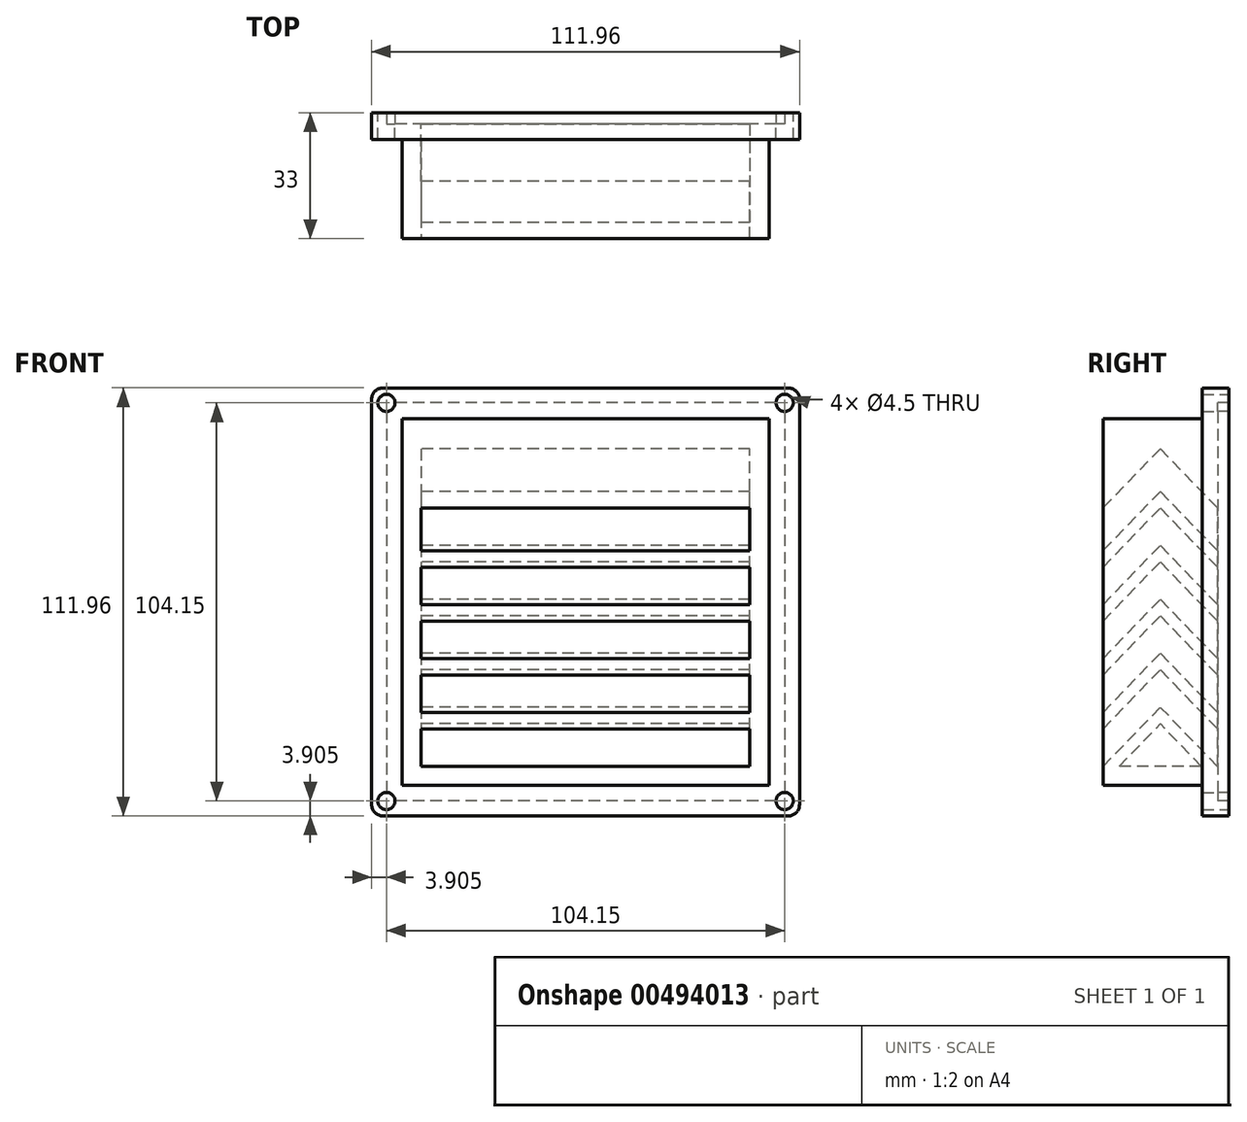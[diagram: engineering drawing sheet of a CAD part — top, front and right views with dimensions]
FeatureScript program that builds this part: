
annotation { "Feature Type Name" : "Feature", "Feature Type Description" : "" }
export const myFeature = defineFeature(function(context is Context, id is Id, definition is map)
    precondition{}
    {
        {
            var Q0;
            Q0=qCreatedBy(makeId("Front.planeOp"),FACE);
            var sketch = newSketch(context, id + "F0", { "sketchPlane" : qUnion([Q0])});
            skPoint(sketch, "E0.middle", {"position": v(0, 0) * mm});
            skCircle(sketch, "E1", {"center": v(-52.08, 52.08) * mm, "radius": 2.25 * mm});
            skCircle(sketch, "E2", {"center": v(52.08, 52.08) * mm, "radius": 2.25 * mm});
            skCircle(sketch, "E3", {"center": v(-52.08, -52.08) * mm, "radius": 2.25 * mm});
            skCircle(sketch, "E4", {"center": v(52.07, -52.08) * mm, "radius": 2.25 * mm});
            skLineSegment(sketch, "E5.bottom", {"start": v(-52.07, 52.08) * mm, "end": v(52.07, 52.08) * mm});
            skLineSegment(sketch, "E5.top", {"start": v(-52.07, -52.08) * mm, "end": v(52.07, -52.08) * mm});
            skLineSegment(sketch, "E5.left", {"start": v(-52.08, 52.08) * mm, "end": v(-52.08, -52.08) * mm});
            skLineSegment(sketch, "E5.right", {"start": v(52.07, 52.08) * mm, "end": v(52.07, -52.08) * mm});
            skLineSegment(sketch, "E6.0", {"start": v(-52.98, 55.98) * mm, "end": v(52.98, 55.98) * mm});
            skLineSegment(sketch, "E6.1", {"start": v(-55.98, 52.98) * mm, "end": v(-55.98, -52.98) * mm});
            skLineSegment(sketch, "E6.2", {"start": v(-52.98, -55.98) * mm, "end": v(52.98, -55.98) * mm});
            skLineSegment(sketch, "E6.3", {"start": v(55.98, 52.98) * mm, "end": v(55.98, -52.98) * mm});
            skPoint(sketch, "E7.visualSharp", {"position": v(-55.98, 55.98) * mm});
            skArc(sketch, "E7.filletArc", {"start": v(-52.98, 55.98) * mm, "mid": v(-55.1, 55.1) * mm, "end": v(-55.98, 52.98) * mm});
            skPoint(sketch, "E8.visualSharp", {"position": v(55.98, 55.98) * mm});
            skArc(sketch, "E8.filletArc", {"start": v(55.98, 52.98) * mm, "mid": v(55.1, 55.1) * mm, "end": v(52.98, 55.98) * mm});
            skPoint(sketch, "E9.visualSharp", {"position": v(55.98, -55.98) * mm});
            skArc(sketch, "E9.filletArc", {"start": v(52.98, -55.98) * mm, "mid": v(55.1, -55.1) * mm, "end": v(55.98, -52.98) * mm});
            skPoint(sketch, "E10.visualSharp", {"position": v(-55.98, -55.98) * mm});
            skArc(sketch, "E10.filletArc", {"start": v(-55.98, -52.98) * mm, "mid": v(-55.1, -55.1) * mm, "end": v(-52.98, -55.98) * mm});
            skLineSegment(sketch, "E11.0", {"start": v(-47.97, 47.97) * mm, "end": v(47.97, 47.97) * mm});
            skLineSegment(sketch, "E11.1", {"start": v(-47.97, 47.97) * mm, "end": v(-47.97, -47.97) * mm});
            skLineSegment(sketch, "E11.2", {"start": v(-47.97, -47.97) * mm, "end": v(47.97, -47.97) * mm});
            skLineSegment(sketch, "E11.3", {"start": v(47.97, 47.97) * mm, "end": v(47.97, -47.97) * mm});
            skSolve(sketch);
        }
        {
            var Q0;
            Q0=makeQuery(id+"F0.imprint","IMPRINT",FACE,{"disambiguationData":[TD([[makeQuery(id+"F0.imprint","IMPRINT",EDGE,{"derivedFrom":sQuery(id+"F0.wireOp",EDGE,"E6.0")}),-1.0]])]});
            var Q1;
            {var subQ5=sQuery(id+"F0.wireOp",EDGE,"E1");var subQ7=sQuery(id+"F0.wireOp",EDGE,"E5.bottom");var subQ15=makeQuery(id+"F0.imprint","INTERSECT",VERTEX,{"derivedFrom":[subQ5,subQ7]});Q1=makeQuery(id+"F0.imprint","IMPRINT",FACE,{"disambiguationData":[TD([[makeQuery(id+"F0.imprint","IMPRINT",EDGE,{"disambiguationData":[TD([[subQ15,1.0]])],"derivedFrom":subQ5}),-1.0]])]});}
            extrude(context, id + "F1", {"entities" : qUnion([Q0, Q1]), "depth" : 4 * mm});
        }
        {
            var Q0;
            Q0=makeQuery(id+"F0.imprint","IMPRINT",FACE,{"disambiguationData":[TD([[makeQuery(id+"F0.imprint","IMPRINT",EDGE,{"derivedFrom":sQuery(id+"F0.wireOp",EDGE,"E11.0")}),-1.0]])]});
            extrude(context, id + "F2", {"entities" : qUnion([Q0]), "operationType" : NewBodyOperationType.ADD, "depth" : 30 * mm});
        }
        {
            var Q0;
            Q0=makeQuery(id+"F2.opExtrude","CAP_FACE",FACE,{"disambiguationData":[OSD([sQuery(id+"F0.wireOp",EDGE,"E11.0"),sQuery(id+"F0.wireOp",EDGE,"E11.1"),sQuery(id+"F0.wireOp",EDGE,"E11.2"),sQuery(id+"F0.wireOp",EDGE,"E11.3")])],"isStart":false});
            var sketch = newSketch(context, id + "F3", { "sketchPlane" : qUnion([Q0])});
            skLineSegment(sketch, "E12.0", {"start": v(42.97, -42.97) * mm, "end": v(42.97, 42.97) * mm});
            skLineSegment(sketch, "E12.1", {"start": v(-42.97, -42.97) * mm, "end": v(42.97, -42.97) * mm});
            skLineSegment(sketch, "E12.2", {"start": v(-42.97, 42.97) * mm, "end": v(-42.97, -42.97) * mm});
            skLineSegment(sketch, "E12.3", {"start": v(42.97, 42.97) * mm, "end": v(-42.97, 42.97) * mm});
            skSolve(sketch);
        }
        {
            var Q0;
            Q0=makeQuery(id+"F3.imprint","IMPRINT",FACE,{"disambiguationData":[TD([[makeQuery(id+"F3.imprint","IMPRINT",EDGE,{"derivedFrom":sQuery(id+"F3.wireOp",EDGE,"E12.0")}),1.0]])]});
            extrude(context, id + "F4", {"entities" : qUnion([Q0]), "operationType" : NewBodyOperationType.REMOVE, "oppositeDirection" : true, "depth" : 40 * mm});
        }
        {
            var Q0;
            Q0=makeQuery(id+"F4.boolean.opBoolean","COPY",FACE,{"derivedFrom":makeQuery(id+"F4.opExtrude","SWEPT_FACE",FACE,{"disambiguationData":[OSD([sQuery(id+"F3.wireOp",EDGE,"E12.2")])]})});
            var sketch = newSketch(context, id + "F5", { "sketchPlane" : qUnion([Q0])});
            skLineSegment(sketch, "E13", {"start": v(-15, 44.38) * mm, "end": v(-30, 28.88) * mm});
            skLineSegment(sketch, "E14", {"start": v(-30, 27.47) * mm, "end": v(-30, 23.12) * mm});
            skLineSegment(sketch, "E15", {"start": v(-15, 40.03) * mm, "end": v(-30, 24.52) * mm});
            skLineSegment(sketch, "E16.MirrorCS", {"start": v(0, 28.88) * mm, "end": v(0, 24.52) * mm});
            skLineSegment(sketch, "E17.MirrorCS", {"start": v(-15, 44.38) * mm, "end": v(0, 28.88) * mm});
            skLineSegment(sketch, "E18.MirrorCS", {"start": v(-15, 40.03) * mm, "end": v(0, 24.52) * mm});
            skLineSegment(sketch, "E19.1.0.0", {"start": v(-15, 28.88) * mm, "end": v(-30, 13.37) * mm});
            skLineSegment(sketch, "E19.1.0.1", {"start": v(-15, 28.88) * mm, "end": v(0, 13.37) * mm});
            skLineSegment(sketch, "E19.1.0.2", {"start": v(-15, 24.52) * mm, "end": v(-30, 9.02) * mm});
            skLineSegment(sketch, "E19.1.0.3", {"start": v(-15, 24.52) * mm, "end": v(0, 9.02) * mm});
            skLineSegment(sketch, "E19.1.0.4", {"start": v(-30, 13.37) * mm, "end": v(-30, 9.02) * mm});
            skLineSegment(sketch, "E19.1.0.5", {"start": v(0, 13.37) * mm, "end": v(0, 9.02) * mm});
            skLineSegment(sketch, "E19.2.0.0", {"start": v(-15, 14.78) * mm, "end": v(-30, -0.73) * mm});
            skLineSegment(sketch, "E19.2.0.1", {"start": v(-15, 14.78) * mm, "end": v(0, -0.73) * mm});
            skLineSegment(sketch, "E19.2.0.2", {"start": v(-15, 10.42) * mm, "end": v(-30, -5.08) * mm});
            skLineSegment(sketch, "E19.2.0.3", {"start": v(-15, 10.42) * mm, "end": v(0, -5.08) * mm});
            skLineSegment(sketch, "E19.2.0.4", {"start": v(-30, -0.73) * mm, "end": v(-30, -5.08) * mm});
            skLineSegment(sketch, "E19.2.0.5", {"start": v(0, -0.73) * mm, "end": v(0, -5.08) * mm});
            skLineSegment(sketch, "E19.3.0.0", {"start": v(-15, 0.68) * mm, "end": v(-30, -14.83) * mm});
            skLineSegment(sketch, "E19.3.0.1", {"start": v(-15, 0.68) * mm, "end": v(0, -14.83) * mm});
            skLineSegment(sketch, "E19.3.0.2", {"start": v(-15, -3.68) * mm, "end": v(-30, -19.18) * mm});
            skLineSegment(sketch, "E19.3.0.3", {"start": v(-15, -3.68) * mm, "end": v(0, -19.18) * mm});
            skLineSegment(sketch, "E19.3.0.4", {"start": v(-30, -14.83) * mm, "end": v(-30, -19.18) * mm});
            skLineSegment(sketch, "E19.3.0.5", {"start": v(0, -14.83) * mm, "end": v(0, -19.18) * mm});
            skLineSegment(sketch, "E19.4.0.0", {"start": v(-15, -13.42) * mm, "end": v(-30, -28.93) * mm});
            skLineSegment(sketch, "E19.4.0.1", {"start": v(-15, -13.42) * mm, "end": v(0, -28.93) * mm});
            skLineSegment(sketch, "E19.4.0.2", {"start": v(-15, -17.78) * mm, "end": v(-30, -33.28) * mm});
            skLineSegment(sketch, "E19.4.0.3", {"start": v(-15, -17.78) * mm, "end": v(0, -33.28) * mm});
            skLineSegment(sketch, "E19.4.0.4", {"start": v(-30, -28.93) * mm, "end": v(-30, -33.28) * mm});
            skLineSegment(sketch, "E19.4.0.5", {"start": v(0, -28.93) * mm, "end": v(0, -33.28) * mm});
            skLineSegment(sketch, "E19.5.0.0", {"start": v(-15, -27.52) * mm, "end": v(-30, -43.03) * mm});
            skLineSegment(sketch, "E19.5.0.1", {"start": v(-15, -27.52) * mm, "end": v(0, -43.03) * mm});
            skLineSegment(sketch, "E19.5.0.2", {"start": v(-15, -31.88) * mm, "end": v(-30, -47.38) * mm});
            skLineSegment(sketch, "E19.5.0.3", {"start": v(-15, -31.88) * mm, "end": v(0, -47.38) * mm});
            skLineSegment(sketch, "E19.5.0.4", {"start": v(-30, -43.03) * mm, "end": v(-30, -47.38) * mm});
            skLineSegment(sketch, "E19.5.0.5", {"start": v(0, -43.03) * mm, "end": v(0, -47.38) * mm});
            skLineSegment(sketch, "E19.direction1", {"start": v(-30, 28.88) * mm, "end": v(-30, 14.78) * mm, "construction": true});
            skSolve(sketch);
        }
        {
            var Q0;
            {var subQ4=sQuery(id+"F5.wireOp",EDGE,"E19.1.0.1");Q0=makeQuery(id+"F5.imprint","IMPRINT",FACE,{"disambiguationData":[TD([[makeQuery(id+"F5.imprint","IMPRINT",EDGE,{"derivedFrom":subQ4}),-1.0]])]});}
            var Q1;
            {var subQ4=sQuery(id+"F5.wireOp",EDGE,"E19.2.0.1");Q1=makeQuery(id+"F5.imprint","IMPRINT",FACE,{"disambiguationData":[TD([[makeQuery(id+"F5.imprint","IMPRINT",EDGE,{"derivedFrom":subQ4}),-1.0]])]});}
            var Q2;
            {var subQ4=sQuery(id+"F5.wireOp",EDGE,"E19.3.0.1");Q2=makeQuery(id+"F5.imprint","IMPRINT",FACE,{"disambiguationData":[TD([[makeQuery(id+"F5.imprint","IMPRINT",EDGE,{"derivedFrom":subQ4}),-1.0]])]});}
            var Q3;
            {var subQ6=sQuery(id+"F5.wireOp",EDGE,"E19.4.0.1");Q3=makeQuery(id+"F5.imprint","IMPRINT",FACE,{"disambiguationData":[TD([[makeQuery(id+"F5.imprint","IMPRINT",EDGE,{"derivedFrom":subQ6}),-1.0]])]});}
            var Q4;
            {var subQ6=sQuery(id+"F5.wireOp",EDGE,"E19.5.0.1");var subQ7=sQuery(id+"F5.wireOp",EDGE,"E19.5.0.0");var subQ8=makeQuery(id+"F5.imprint","INTERSECT",VERTEX,{"derivedFrom":[subQ7,subQ6]});Q4=makeQuery(id+"F5.imprint","IMPRINT",FACE,{"disambiguationData":[TD([[makeQuery(id+"F5.imprint","IMPRINT",EDGE,{"disambiguationData":[TD([[subQ8,-1.0]])],"derivedFrom":subQ7}),1.0]])]});}
            extrude(context, id + "F6", {"entities" : qUnion([Q0, Q1, Q2, Q3, Q4]), "operationType" : NewBodyOperationType.ADD, "depth" : 86.5 * mm});
        }
        {
            var Q0;
            {var subQ1=sQuery(id+"F5.wireOp",EDGE,"E15");Q0=makeQuery(id+"F5.imprint","IMPRINT",FACE,{"disambiguationData":[TD([[makeQuery(id+"F5.imprint","IMPRINT",EDGE,{"derivedFrom":subQ1}),-1.0]])]});}
            extrude(context, id + "F7", {"entities" : qUnion([Q0]), "operationType" : NewBodyOperationType.ADD, "depth" : 86.5 * mm});
        }
        {
            var Q0;
            {var subQ1=sQuery(id+"F3.wireOp",EDGE,"E12.2");var subQ4=makeQuery(id+"F4.boolean.opBoolean","COPY",FACE,{"derivedFrom":makeQuery(id+"F4.opExtrude","SWEPT_FACE",FACE,{"disambiguationData":[OSD([sQuery(id+"F3.wireOp",EDGE,"E12.3")])]})});Q0=makeQuery(id+"F7.boolean.opBoolean","SPLIT",FACE,{"disambiguationData":[TD([makeQuery(id+"F7.opExtrude","SWEPT_FACE",FACE,{"disambiguationData":[OSD([sQuery(id+"F5.wireOp",EDGE,"E13")])]})])],"derivedFrom":makeQuery(id+"F6.boolean.opBoolean","SPLIT",FACE,{"disambiguationData":[TD([subQ4])],"derivedFrom":makeQuery(id+"F4.boolean.opBoolean","COPY",FACE,{"derivedFrom":makeQuery(id+"F4.opExtrude","SWEPT_FACE",FACE,{"disambiguationData":[OSD([subQ1])]})})})});}
            extrude(context, id + "F8", {"entities" : qUnion([Q0]), "operationType" : NewBodyOperationType.ADD, "depth" : 86.5 * mm});
        }
        {
            var Q0;
            {var subQ0=makeQuery(id+"F4.boolean.opBoolean","COPY",FACE,{"derivedFrom":makeQuery(id+"F4.opExtrude","SWEPT_FACE",FACE,{"disambiguationData":[OSD([sQuery(id+"F3.wireOp",EDGE,"E12.3")])]})});var subQ7=sQuery(id+"F3.wireOp",EDGE,"E12.2");Q0=makeQuery(id+"F7.boolean.opBoolean","SPLIT",FACE,{"disambiguationData":[TD([makeQuery(id+"F7.opExtrude","SWEPT_FACE",FACE,{"disambiguationData":[OSD([sQuery(id+"F5.wireOp",EDGE,"E17.MirrorCS")])]})])],"derivedFrom":makeQuery(id+"F6.boolean.opBoolean","SPLIT",FACE,{"disambiguationData":[TD([subQ0])],"derivedFrom":makeQuery(id+"F4.boolean.opBoolean","COPY",FACE,{"derivedFrom":makeQuery(id+"F4.opExtrude","SWEPT_FACE",FACE,{"disambiguationData":[OSD([subQ7])]})})})});}
            extrude(context, id + "F9", {"entities" : qUnion([Q0]), "operationType" : NewBodyOperationType.ADD, "depth" : 86.5 * mm});
        }
        {
            var Q0;
            {var subQ0=sQuery(id+"F0.wireOp",EDGE,"E11.3");var subQ1=sQuery(id+"F0.wireOp",EDGE,"E11.2");var subQ2=sQuery(id+"F0.wireOp",EDGE,"E11.1");var subQ3=sQuery(id+"F0.wireOp",EDGE,"E11.0");var subQ4=sQuery(id+"F0.wireOp",EDGE,"E10.filletArc");var subQ5=sQuery(id+"F0.wireOp",EDGE,"E9.filletArc");var subQ6=sQuery(id+"F0.wireOp",EDGE,"E8.filletArc");var subQ7=sQuery(id+"F0.wireOp",EDGE,"E7.filletArc");var subQ8=sQuery(id+"F0.wireOp",EDGE,"E6.3");var subQ9=sQuery(id+"F0.wireOp",EDGE,"E6.2");var subQ10=sQuery(id+"F0.wireOp",EDGE,"E6.1");var subQ11=sQuery(id+"F0.wireOp",EDGE,"E6.0");var subQ12=sQuery(id+"F0.wireOp",EDGE,"E4");var subQ13=sQuery(id+"F0.wireOp",EDGE,"E3");var subQ14=sQuery(id+"F0.wireOp",EDGE,"E2");var subQ15=sQuery(id+"F0.wireOp",EDGE,"E1");Q0=makeQuery(id+"F9.boolean.opBoolean","MERGE",FACE,{"derivedFrom":[makeQuery(id+"F7.boolean.opBoolean","MERGE",FACE,{"derivedFrom":[makeQuery(id+"F2.boolean.opBoolean","MERGE",FACE,{"derivedFrom":[makeQuery(id+"F1.opExtrude","CAP_FACE",FACE,{"disambiguationData":[OSD([subQ15,subQ14,subQ13,subQ12,subQ11,subQ10,subQ9,subQ8,subQ7,subQ6,subQ5,subQ4,subQ3,subQ2,subQ1,subQ0])],"isStart":true}),makeQuery(id+"F2.opExtrude","CAP_FACE",FACE,{"disambiguationData":[OSD([subQ3,subQ2,subQ1,subQ0])],"isStart":true})]}),makeQuery(id+"F7.opExtrude","SWEPT_FACE",FACE,{"disambiguationData":[OSD([sQuery(id+"F5.wireOp",EDGE,"E16.MirrorCS")])]})]}),makeQuery(id+"F9.opExtrude","SWEPT_FACE",FACE,{"disambiguationData":[OSD([subQ15,subQ14,subQ13,subQ12,subQ11,subQ10,subQ9,subQ8,subQ7,subQ6,subQ5,subQ4,subQ3,subQ2,subQ1,subQ0,sQuery(id+"F3.wireOp",EDGE,"E12.2")])]})]});}
            var sketch = newSketch(context, id + "F10", { "sketchPlane" : qUnion([Q0])});
            skLineSegment(sketch, "E20.bottom", {"start": v(-52.08, 52.08) * mm, "end": v(52.08, 52.08) * mm});
            skLineSegment(sketch, "E20.top", {"start": v(-52.08, -52.08) * mm, "end": v(52.08, -52.08) * mm});
            skLineSegment(sketch, "E20.left", {"start": v(-52.08, 52.08) * mm, "end": v(-52.08, -52.08) * mm});
            skLineSegment(sketch, "E20.right", {"start": v(52.08, 52.08) * mm, "end": v(52.08, -52.08) * mm});
            skLineSegment(sketch, "E21.0", {"start": v(-55.98, 55.98) * mm, "end": v(-55.98, -55.98) * mm});
            skLineSegment(sketch, "E21.1", {"start": v(-55.98, 55.98) * mm, "end": v(55.98, 55.98) * mm});
            skLineSegment(sketch, "E21.2", {"start": v(55.98, 55.98) * mm, "end": v(55.98, -55.98) * mm});
            skLineSegment(sketch, "E21.3", {"start": v(-55.98, -55.98) * mm, "end": v(55.98, -55.98) * mm});
            skLineSegment(sketch, "E22.0", {"start": v(-48.9, 48.9) * mm, "end": v(48.9, 48.9) * mm});
            skLineSegment(sketch, "E22.1", {"start": v(-48.9, 48.9) * mm, "end": v(-48.9, -48.9) * mm});
            skLineSegment(sketch, "E22.2", {"start": v(-48.9, -48.9) * mm, "end": v(48.9, -48.9) * mm});
            skLineSegment(sketch, "E22.3", {"start": v(48.9, 48.9) * mm, "end": v(48.9, -48.9) * mm});
            skSolve(sketch);
        }
        {
            var Q0;
            Q0=makeQuery(id+"F10.imprint","IMPRINT",FACE,{"disambiguationData":[TD([[makeQuery(id+"F10.imprint","IMPRINT",EDGE,{"derivedFrom":makeQuery(id+"F1.opExtrude","CAP_EDGE",EDGE,{"disambiguationData":[OSD([sQuery(id+"F0.wireOp",EDGE,"E6.0")])],"isStart":true})}),1.0]])]});
            extrude(context, id + "F11", {"entities" : qUnion([Q0]), "operationType" : NewBodyOperationType.ADD, "depth" : 3 * mm});
        }
    });
